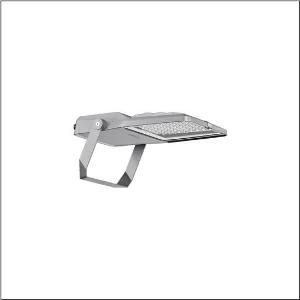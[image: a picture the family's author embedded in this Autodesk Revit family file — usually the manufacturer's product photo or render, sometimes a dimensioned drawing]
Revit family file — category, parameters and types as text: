
# Revit family: floodlight_fl_21_mini___pl61_5xa7775d2c1a_9234
name_source: partatom
category: Lighting Fixtures
units: mm (PartAtom-declared; Revit-internal decimal feet)

## family parameters
Cut with Voids When Loaded = No
Host = Face
Light Source = No
Part Type = Normal
Room Calculation Point = No
Round Connector Dimension = Use Diameter
Shared = No

## types (1)
- --- (1 x LED, 17510 lm, 142.9 W, 3000K)
    Apparent Load = 143 VA
    CIE Flux Codes = 33 65 98 100 100
    Color Rendering = 70
    Color Temperature = 3000K
    Default Elevation = 1800 mm
    Description = Floodlight FL 21 mini, floodlight, primary light control with lens, of PMMA, primary optical cover: protective disc, of toughened safety glass, transparent, light distribution: PL61, light emission: direct distribution, installation type: surface-mounted, LED, High Power LED, rated luminous flux: 17.510lm, luminous efficacy: 123lm/W, light colour: 730, colour temperature: 3000K, control gear: Smart Interface (Zhaga), control: flexible luminous flux parameterisation, time-dependent luminous flux control, constant luminous flux control, overheat protection, pre-setting: logarithmic dimming characteristic, with terminal, 6-pole, mains connection: 220..240V, AC, 50/60Hz, start of lifetime: 143W, end of service life: 151W, reduction: 63W, luminaire housing, of diecast aluminium, powder-coated, SITECO metallic grey (DB 702S), corrosivity category C5 mid according to DIN EN ISO 12944, suitable for swimming pools, chlorine-resistant, sealing non-destructively replaceable, mounting bracket, of steel, galvanised, powder-coated, SITECO metallic grey (DB 702S), Smart Interface above, protection rating (complete): IP66, insulation class (complete): insulation class II (safety insulation), certification: CE, ENEC, VDE, protection symbol: D, impact resistance: IK08, permissible operating ambient temperature: -40..+40°C, permissible operating ambient temperature for outdoor applications: -40..+50°C, standard: DIN EN 12944, LABS conformity tested according to VDMA 24364:2018-05, packaging unit: 1 piece

Light Distribution: PL61
    Height = 70 mm
    Lamp = 1 x LED
    Lamp Light Flux = 17510 lm
    Lamp Power = 142.9 W
    Lamp count = 1
    Length = 485 mm
    Luminous efficacy = 123 lm/W
    Manufacturer = Siteco
    ModVariant = No
    Model = 5XA7775D2C1A
    Mounting Place = Pole
    Mounting Type = Pole annexe
    Number of Poles = 1
    OnlyDefault = Yes
    Power Factor = 1
    Product Name = Floodlight FL 21 mini | PL61
    Product group = floodlight | pylon annexe
    ProductGroupID = 6201
    Protection Class = Protection class II
    Protection Degree = IP 66
    RLX_Detail_Level = 1
    RLX_Emergency_Light_Flux = 0 lm
    RLX_Emergency_Type = 0
    RLX_Emergency_Type_DB = No
    RlxData = <blob elided: 96401 chars, md5=c4361ff1>
    Socket = socket
    Standby Power = 0 W
    System Light Flux = 17510 lm
    System Power = 143 W
    Type Comments = factory setting: luminous flux: 100 % | dim-lin: 254 | 730 mA
    Type Image = l_1006845.jpg
    URL = http://relux.com
    VarID = @adj_172995
    Voltage = 0 V
    Weight = 0.00 kg
    Width = 337 mm

## geometry (parser evidence)
native form markers: Blend x4, Sweep x11
no freeform markers — native parametric forms only
